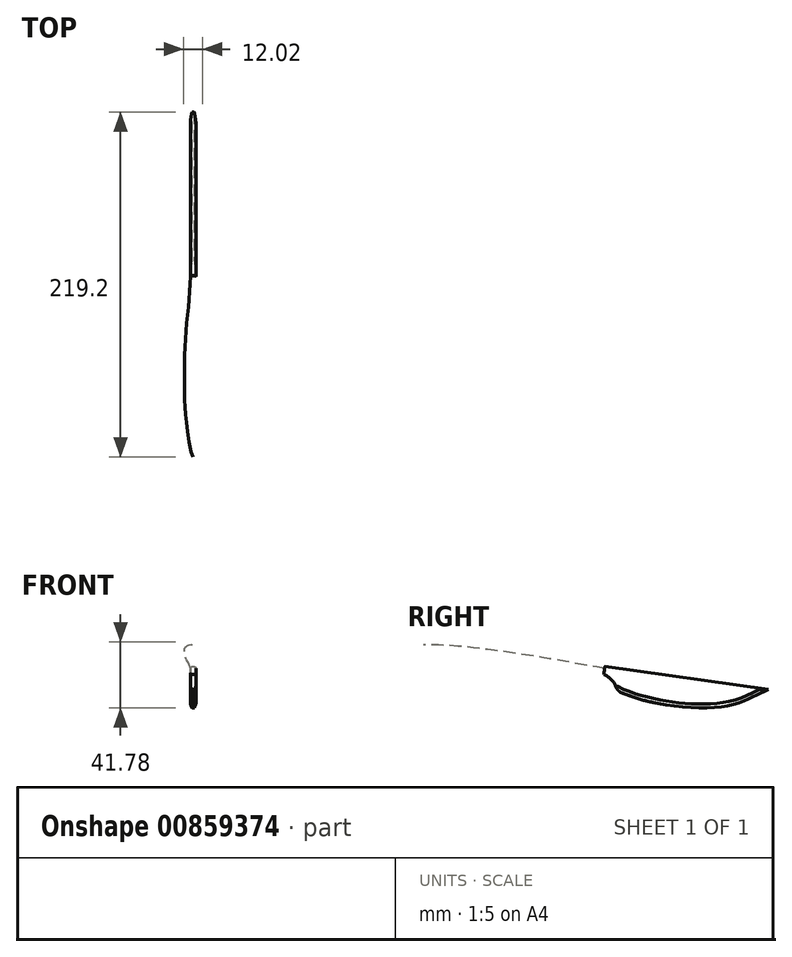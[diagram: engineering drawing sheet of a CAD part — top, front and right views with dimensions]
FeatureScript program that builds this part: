
annotation { "Feature Type Name" : "Feature", "Feature Type Description" : "" }
export const myFeature = defineFeature(function(context is Context, id is Id, definition is map)
    precondition{}
    {
        {
            var Q0;
            Q0=qCreatedBy(makeId("Right.planeOp"),FACE);
            var sketch = newSketch(context, id + "F0", { "sketchPlane" : qUnion([Q0])});
            skLineSegment(sketch, "E0", {"start": v(0, 0) * mm, "end": v(-104.97, 14.75) * mm, "construction": true});
            skLineSegment(sketch, "E1", {"start": v(-105.39, 11.78) * mm, "end": v(-104.55, 17.72) * mm, "construction": true});
            skPoint(sketch, "E2", {"position": v(-104.97, 14.75) * mm});
            skLineSegment(sketch, "E3", {"start": v(-70.15, 3.8) * mm, "end": v(-68.48, 15.68) * mm, "construction": true});
            skPoint(sketch, "E4", {"position": v(-69.32, 9.74) * mm});
            skLineSegment(sketch, "E5", {"start": v(-0.35, -2.48) * mm, "end": v(0.35, 2.48) * mm});
            skPoint(sketch, "E6", {"position": v(0, 0) * mm});
            skLineSegment(sketch, "E7", {"start": v(-104.97, 14.75) * mm, "end": v(-108.93, 15.3) * mm, "construction": true});
            skFitSpline(sketch, "E8", {"points": [v(0.35, 2.48) * mm, v(-68.48, 15.68) * mm, v(-104.55, 17.72) * mm, v(-108.93, 15.3) * mm, v(-105.39, 11.78) * mm, v(-70.15, 3.8) * mm, v(-0.35, -2.48) * mm], "startDerivative": vector(-411.97, 63.91) * mm, "endDerivative": vector(413.63, -52.12) * mm});
            skLineSegment(sketch, "E9", {"start": v(-36.4, -7.45) * mm, "end": v(-32.93, 17.19) * mm, "construction": true});
            skPoint(sketch, "E10", {"position": v(-34.66, 4.87) * mm});
            skPoint(sketch, "E11", {"position": v(-34.12, 8.73) * mm});
            skPoint(sketch, "E12", {"position": v(-35.2, 1.02) * mm});
            skLineSegment(sketch, "E13", {"start": v(0.24, 1.69) * mm, "end": v(-0.25, -1.8) * mm});
            skLineSegment(sketch, "E14", {"start": v(0.35, 2.48) * mm, "end": v(104.33, -12.14) * mm});
            skLineSegment(sketch, "E15", {"start": v(79.57, -8.66) * mm, "end": v(77.62, -22.52) * mm, "construction": true});
            skLineSegment(sketch, "E16", {"start": v(10.25, 1.08) * mm, "end": v(8.3, -12.78) * mm, "construction": true});
            skArc(sketch, "E17", {"start": v(7.75, -10.97) * mm, "mid": v(4.57, -5.9) * mm, "end": v(-0.35, -2.48) * mm});
            skFitSpline(sketch, "E18", {"points": [v(8.3, -12.78) * mm, v(77.62, -22.52) * mm, v(104.33, -12.14) * mm], "startDerivative": vector(89.85, -45.1) * mm, "endDerivative": vector(59.89, 23.01) * mm});
            skArc(sketch, "E19.filletArc", {"start": v(7.75, -10.97) * mm, "mid": v(8.78, -12.62) * mm, "end": v(10.35, -13.76) * mm});
            skSolve(sketch);
        }
        {
            var Q0;
            {var subQ2=sQuery(id+"F0.wireOp",EDGE,"E5");Q0=makeQuery(id+"F0.imprint","IMPRINT",FACE,{"disambiguationData":[TD([[makeQuery(id+"F0.imprint","IMPRINT",EDGE,{"derivedFrom":subQ2}),-1.0]])]});}
            extrude(context, id + "F1", {"entities" : qUnion([Q0]), "endBound" : BoundingType.SYMMETRIC, "depth" : 3.5 * mm, "offsetDistance" : 25 * mm});
        }
        {
            var Q0;
            Q0=makeQuery(id+"F1.opExtrude","CAP_EDGE",EDGE,{"disambiguationData":[OSD([sQuery(id+"F0.wireOp",EDGE,"E14")])],"isStart":false});
            var Q1;
            Q1=makeQuery(id+"F1.opExtrude","CAP_EDGE",EDGE,{"disambiguationData":[OSD([sQuery(id+"F0.wireOp",EDGE,"E14")])],"isStart":true});
            fillet(context, id + "F2", {"entities" : qUnion([Q0, Q1]), "radius" : 1 * mm, "tangentPropagation" : true, "allowEdgeOverflow" : false});
        }
        {
            var Q0;
            Q0=makeQuery(id+"F1.opExtrude","CAP_EDGE",EDGE,{"disambiguationData":[OSD([sQuery(id+"F0.wireOp",EDGE,"E17")])],"isStart":false});
            var Q1;
            Q1=makeQuery(id+"F1.opExtrude","CAP_EDGE",EDGE,{"disambiguationData":[OSD([sQuery(id+"F0.wireOp",EDGE,"E17")])],"isStart":true});
            fillet(context, id + "F3", {"entities" : qUnion([Q0, Q1]), "radius" : 1 * mm, "allowEdgeOverflow" : false});
        }
        {
            var Q0;
            Q0=makeQuery(id+"F1.opExtrude","CAP_EDGE",EDGE,{"disambiguationData":[OSD([sQuery(id+"F0.wireOp",EDGE,"E18")])],"isStart":false});
            var Q1;
            Q1=makeQuery(id+"F1.opExtrude","CAP_EDGE",EDGE,{"disambiguationData":[OSD([sQuery(id+"F0.wireOp",EDGE,"E18")])],"isStart":true});
            chamfer(context, id + "F4", {"entities" : qUnion([Q0, Q1]), "chamferType" : ChamferType.TWO_OFFSETS, "width1" : 2.5 * mm, "oppositeDirection" : false, "width2" : 1 * mm});
        }
        {
            var Q0;
            Q0=sQuery(id+"F0.wireOp",EDGE,"E9");
            cPlane(context, id + "F5", {"entities" : qUnion([Q0]), "cplaneType" : CPlaneType.LINE_ANGLE, "offset" : 25 * mm, "angle" : 90 * degree, "width" : 150 * mm, "height" : 150 * mm});
        }
        {
            var Q0;
            Q0=sQuery(id+"F0.wireOp",EDGE,"E3");
            cPlane(context, id + "F6", {"entities" : qUnion([Q0]), "cplaneType" : CPlaneType.LINE_ANGLE, "offset" : 25 * mm, "angle" : 90 * degree, "width" : 150 * mm, "height" : 150 * mm});
        }
        {
            var Q0;
            Q0=sQuery(id+"F0.wireOp",EDGE,"E1");
            cPlane(context, id + "F7", {"entities" : qUnion([Q0]), "cplaneType" : CPlaneType.LINE_ANGLE, "offset" : 25 * mm, "angle" : 90 * degree, "width" : 150 * mm, "height" : 150 * mm});
        }
        {
            var Q0;
            Q0=qCreatedBy(id+"F7.planeOp",FACE);
            var sketch = newSketch(context, id + "F8", { "sketchPlane" : qUnion([Q0])});
            skEllipse(sketch, "E20", {"center": v(0, 0) * mm, "majorRadius": 3 * mm, "minorRadius": 3 * mm, "majorAxis": v(1, 0)});
            skLineSegment(sketch, "E21", {"start": v(3, 0) * mm, "end": v(-3, 0) * mm, "construction": true});
            skLineSegment(sketch, "E22", {"start": v(0, 3) * mm, "end": v(0, -3) * mm, "construction": true});
            skSolve(sketch);
        }
        {
            var Q0;
            Q0=qCreatedBy(id+"F6.planeOp",FACE);
            var sketch = newSketch(context, id + "F9", { "sketchPlane" : qUnion([Q0])});
            skEllipse(sketch, "E23", {"center": v(0, 0) * mm, "majorRadius": 6 * mm, "minorRadius": 7 * mm, "majorAxis": v(1, 0)});
            skLineSegment(sketch, "E24", {"start": v(0, 7) * mm, "end": v(0, -7) * mm, "construction": true});
            skLineSegment(sketch, "E25", {"start": v(-6, 0) * mm, "end": v(6, 0) * mm, "construction": true});
            skSolve(sketch);
        }
        {
            var Q0;
            Q0=qCreatedBy(id+"F5.planeOp",FACE);
            var sketch = newSketch(context, id + "F10", { "sketchPlane" : qUnion([Q0])});
            skEllipse(sketch, "E26", {"center": v(0, 0) * mm, "majorRadius": 5 * mm, "minorRadius": 6 * mm, "majorAxis": v(1, 0)});
            skLineSegment(sketch, "E27", {"start": v(-5, 0) * mm, "end": v(5, 0) * mm, "construction": true});
            skLineSegment(sketch, "E28", {"start": v(0, 6) * mm, "end": v(0, -6) * mm, "construction": true});
            skSolve(sketch);
        }
        {
            var Q0;
            Q0=qCreatedBy(id+"F7.planeOp",FACE);
            cPlane(context, id + "F11", {"entities" : qUnion([Q0]), "cplaneType" : CPlaneType.OFFSET, "offset" : 10 * mm, "oppositeDirection" : true, "width" : 150 * mm, "height" : 150 * mm});
        }
        {
            var Q0;
            Q0=qCreatedBy(id+"F11.planeOp",FACE);
            var sketch = newSketch(context, id + "F12", { "sketchPlane" : qUnion([Q0])});
            skCircle(sketch, "E29", {"center": v(0, 0) * mm, "radius": 0.12 * mm});
            skSolve(sketch);
        }
        {
            var Q1;
            Q1=makeQuery(id+"F1.opExtrude","SWEPT_FACE",FACE,{"disambiguationData":[OSD([sQuery(id+"F0.wireOp",EDGE,"E5"),sQuery(id+"F0.wireOp",EDGE,"E13")])]});
            var Q2;
            Q2=makeQuery(id+"F10.imprint","IMPRINT",FACE,{"disambiguationData":[TD([[makeQuery(id+"F10.imprint","IMPRINT",EDGE,{"derivedFrom":sQuery(id+"F10.wireOp",EDGE,"E26")}),1.0]])]});
            var Q3;
            Q3=makeQuery(id+"F9.imprint","IMPRINT",FACE,{"disambiguationData":[TD([[makeQuery(id+"F9.imprint","IMPRINT",EDGE,{"derivedFrom":sQuery(id+"F9.wireOp",EDGE,"E23")}),1.0]])]});
            var Q4;
            Q4=makeQuery(id+"F8.imprint","IMPRINT",FACE,{"disambiguationData":[TD([[makeQuery(id+"F8.imprint","IMPRINT",EDGE,{"derivedFrom":sQuery(id+"F8.wireOp",EDGE,"E20")}),1.0]])]});
            var Q5;
            Q5=sQuery(id+"F12.wireOp",VERTEX,"E29.center");
            loft(context, id + "F13", {"operationType" : NewBodyOperationType.ADD, "startCondition" : LoftEndDerivativeType.NORMAL_TO_PROFILE, "startMagnitude" : 1, "endCondition" : LoftEndDerivativeType.TANGENT_TO_PROFILE, "endMagnitude" : 1, "sheetProfilesArray" : [{ "sheetProfileEntities" : qUnion([Q1]) }, { "sheetProfileEntities" : qUnion([Q2]) }, { "sheetProfileEntities" : qUnion([Q3]) }, { "sheetProfileEntities" : qUnion([Q4]) }, { "sheetProfileEntities" : qUnion([Q5]) }]});
        }
    });
